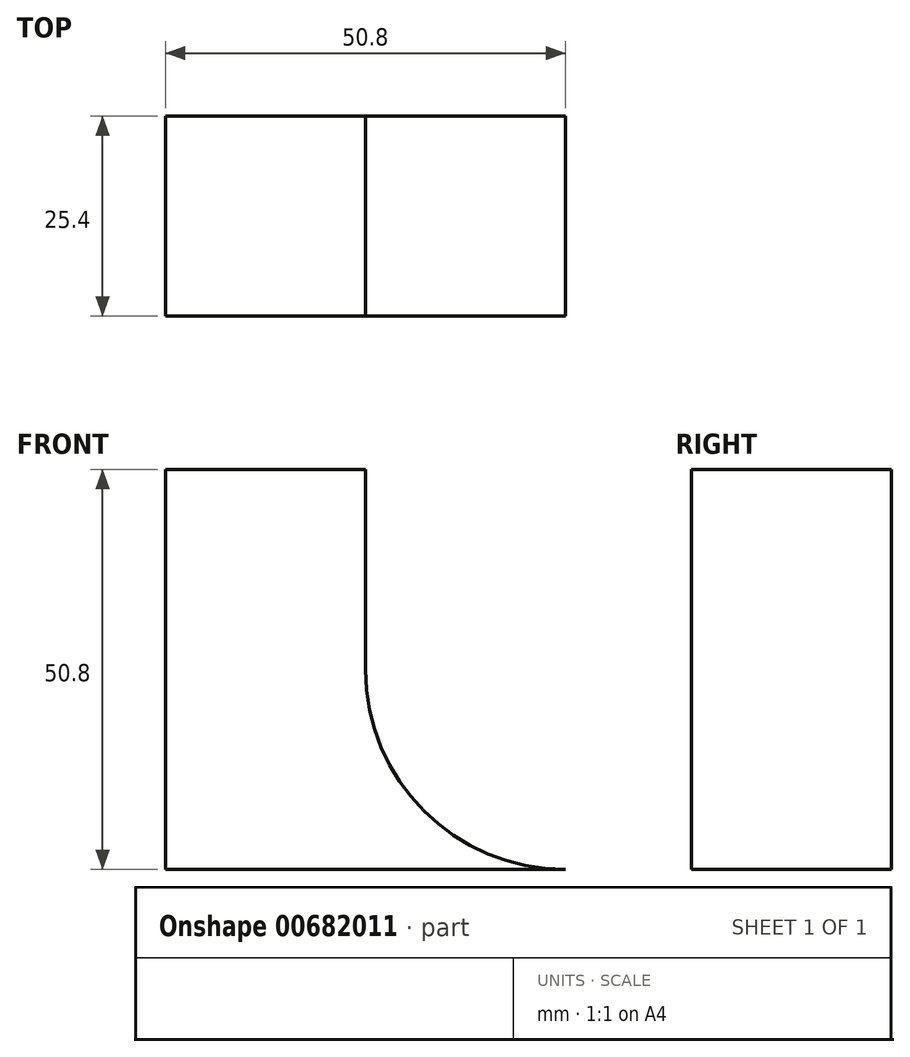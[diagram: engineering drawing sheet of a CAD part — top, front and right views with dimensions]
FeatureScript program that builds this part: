
annotation { "Feature Type Name" : "Feature", "Feature Type Description" : "" }
export const myFeature = defineFeature(function(context is Context, id is Id, definition is map)
    precondition{}
    {
        {
            var Q0;
            Q0=qCreatedBy(makeId("Front.planeOp"),FACE);
            var sketch = newSketch(context, id + "F0", { "sketchPlane" : qUnion([Q0])});
            skLineSegment(sketch, "E0", {"start": v(0, 0) * mm, "end": v(-50.8, 0) * mm});
            skLineSegment(sketch, "E1", {"start": v(-50.8, 0) * mm, "end": v(-50.8, 50.8) * mm});
            skLineSegment(sketch, "E2", {"start": v(-50.8, 50.8) * mm, "end": v(-25.4, 50.8) * mm});
            skLineSegment(sketch, "E3", {"start": v(-25.4, 50.8) * mm, "end": v(-25.4, 25.4) * mm});
            skArc(sketch, "E4", {"start": v(-25.4, 25.4) * mm, "mid": v(-17.96, 7.44) * mm, "end": v(0, 0) * mm});
            skSolve(sketch);
        }
        {
            var Q0;
            Q0 = qSketchRegion(id + "F0", true);
            extrude(context, id + "F1", {"entities" : qUnion([Q0]), "depth" : 25.4 * mm, "offsetDistance" : 25.4 * mm});
        }
    });
